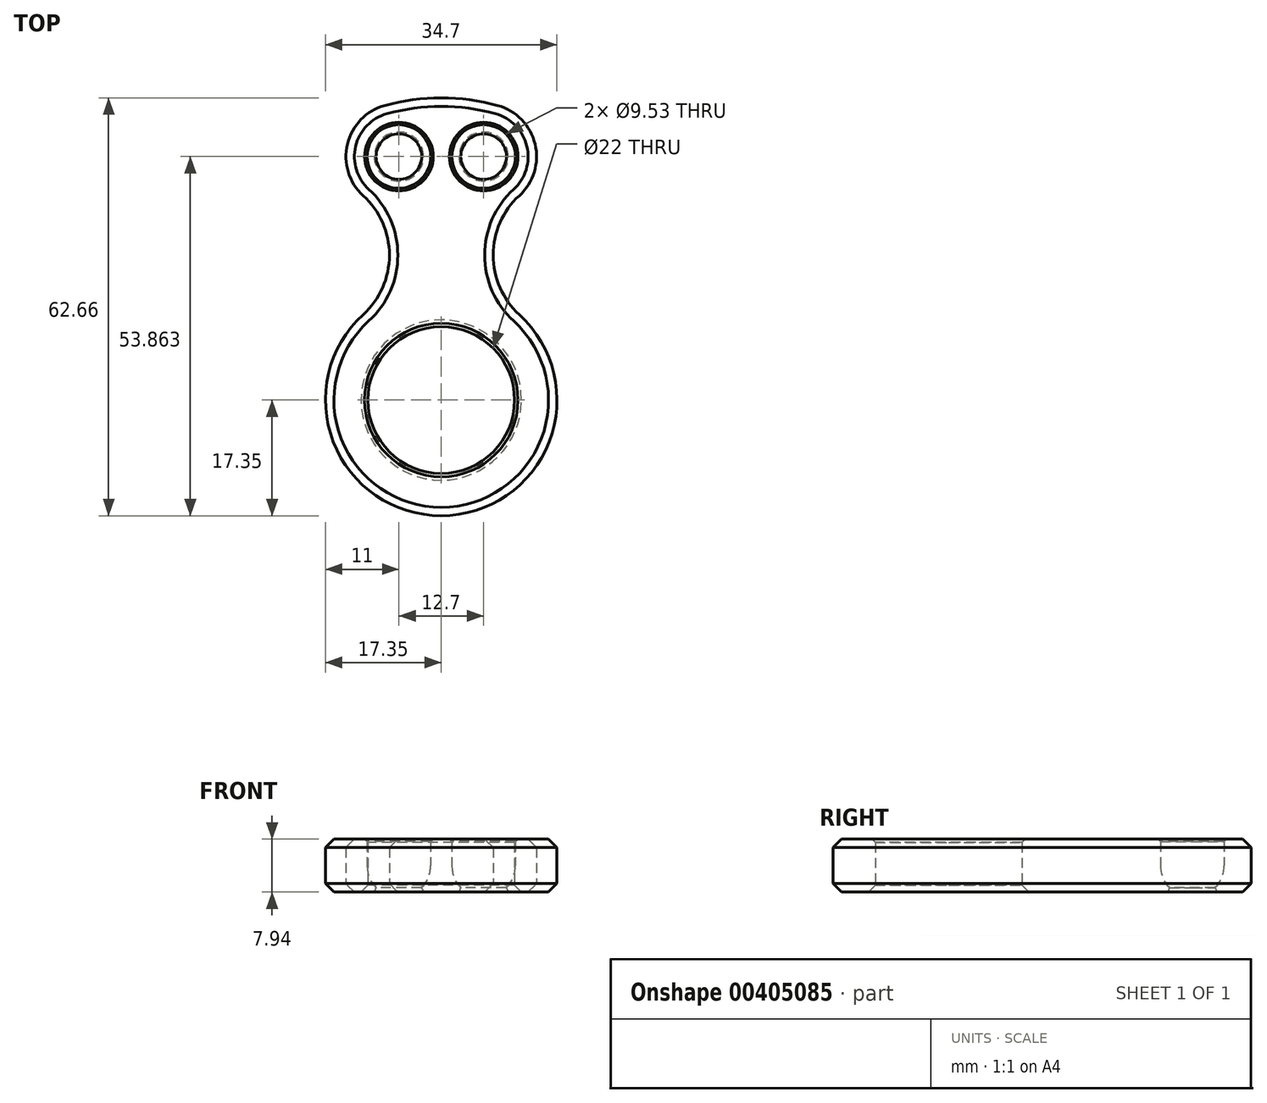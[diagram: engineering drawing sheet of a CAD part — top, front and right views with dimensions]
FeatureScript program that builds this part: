
annotation { "Feature Type Name" : "Feature", "Feature Type Description" : "" }
export const myFeature = defineFeature(function(context is Context, id is Id, definition is map)
    precondition{}
    {
        {
            var Q0;
            Q0=qCreatedBy(makeId("Top.planeOp"),FACE);
            var sketch = newSketch(context, id + "F0", { "sketchPlane" : qUnion([Q0])});
            skCircle(sketch, "E0", {"center": v(0, 0) * mm, "radius": 11 * mm});
            skCircle(sketch, "E1", {"center": v(0, 0) * mm, "radius": 17.35 * mm});
            skSolve(sketch);
        }
        {
            var Q0;
            Q0 = qSketchRegion(id + "F0", true);
            extrude(context, id + "F1", {"entities" : qUnion([Q0]), "depth" : 7.94 * mm});
        }
        {
            var Q0;
            Q0=qCreatedBy(makeId("Top.planeOp"),FACE);
            var sketch = newSketch(context, id + "F2", { "sketchPlane" : qUnion([Q0])});
            skCircle(sketch, "E2", {"center": v(-6.35, 36.51) * mm, "radius": 4.76 * mm});
            skArc(sketch, "E3.0", {"start": v(11.7, 12.8) * mm, "mid": v(0, 17.35) * mm, "end": v(-11.7, 12.8) * mm});
            skPoint(sketch, "E4", {"position": v(-6.35, 41.28) * mm});
            skCircle(sketch, "E5", {"center": v(6.35, 36.51) * mm, "radius": 4.76 * mm});
            skLineSegment(sketch, "E6", {"start": v(-6.35, 36.51) * mm, "end": v(6.35, 36.51) * mm, "construction": true});
            skLineSegment(sketch, "E7", {"start": v(0, 36.51) * mm, "end": v(0, 0) * mm, "construction": true});
            skLineSegment(sketch, "E8", {"start": v(-6.35, 41.28) * mm, "end": v(-6.35, 36.51) * mm, "construction": true});
            skArc(sketch, "E9", {"start": v(0, 31.75) * mm, "mid": v(1.59, 36.51) * mm, "end": v(0, 41.28) * mm, "construction": true});
            skArc(sketch, "E10", {"start": v(11.7, 30.65) * mm, "mid": v(14.07, 38.36) * mm, "end": v(8.47, 44.16) * mm});
            skArc(sketch, "E11", {"start": v(-11.7, 12.8) * mm, "mid": v(-7.77, 21.73) * mm, "end": v(-11.7, 30.65) * mm});
            skArc(sketch, "E12", {"start": v(11.7, 30.65) * mm, "mid": v(7.77, 21.73) * mm, "end": v(11.7, 12.8) * mm});
            skLineSegment(sketch, "E13", {"start": v(6.35, 36.51) * mm, "end": v(6.35, 41.28) * mm, "construction": true});
            skArc(sketch, "E14", {"start": v(8.47, 44.16) * mm, "mid": v(0, 45.31) * mm, "end": v(-8.47, 44.16) * mm});
            skArc(sketch, "E15.trimOffspring", {"start": v(-8.47, 44.16) * mm, "mid": v(-14.07, 38.36) * mm, "end": v(-11.7, 30.65) * mm});
            skArc(sketch, "E16.trimOffspring", {"start": v(0, 41.28) * mm, "mid": v(-1.59, 36.51) * mm, "end": v(0, 31.75) * mm, "construction": true});
            skSolve(sketch);
        }
        {
            var Q0;
            Q0 = qSketchRegion(id + "F2", true);
            var Q1;
            Q1=makeQuery(id+"F1.opExtrude","CAP_FACE",FACE,{"disambiguationData":[OSD([sQuery(id+"F0.wireOp",EDGE,"E0"),sQuery(id+"F0.wireOp",EDGE,"E1")])],"isStart":false});
            extrude(context, id + "F3", {"entities" : qUnion([Q0]), "operationType" : NewBodyOperationType.ADD, "endBound" : BoundingType.UP_TO_SURFACE, "endBoundEntityFace" : qUnion([Q1]), "depth" : 25.4 * mm});
        }
        {
            var Q0;
            Q0=qCreatedBy(makeId("Right.planeOp"),FACE);
            var Q1;
            Q1=sQuery(id+"F2.wireOp",VERTEX,"E6.start");
            cPlane(context, id + "F4", {"entities" : qUnion([Q0, Q1]), "cplaneType" : CPlaneType.PLANE_POINT, "offset" : 25.4 * mm, "width" : 152.4 * mm, "height" : 152.4 * mm});
        }
        {
            var Q0;
            Q0=qCreatedBy(makeId("Right.planeOp"),FACE);
            var Q1;
            Q1=sQuery(id+"F2.wireOp",VERTEX,"E6.end");
            cPlane(context, id + "F5", {"entities" : qUnion([Q0, Q1]), "cplaneType" : CPlaneType.PLANE_POINT, "offset" : 25.4 * mm, "width" : 152.4 * mm, "height" : 152.4 * mm});
        }
        {
            var Q0;
            Q0=qCreatedBy(id+"F4.planeOp",FACE);
            var sketch = newSketch(context, id + "F6", { "sketchPlane" : qUnion([Q0])});
            skArc(sketch, "E17", {"start": v(36.51, -0.8) * mm, "mid": v(37.89, -0.6) * mm, "end": v(39.15, 0) * mm, "construction": true});
            skLineSegment(sketch, "E18", {"start": v(41.28, 3.97) * mm, "end": v(41.28, 0) * mm});
            skLineSegment(sketch, "E19", {"start": v(36.51, 3.97) * mm, "end": v(36.51, 0) * mm, "construction": true});
            skLineSegment(sketch, "E20", {"start": v(0, 7.94) * mm, "end": v(0, 0) * mm, "construction": true});
            skLineSegment(sketch, "E21", {"start": v(0, 3.97) * mm, "end": v(36.51, 3.97) * mm, "construction": true});
            skLineSegment(sketch, "E22", {"start": v(39.15, 0) * mm, "end": v(41.28, 0) * mm});
            skArc(sketch, "E23", {"start": v(39.15, 0) * mm, "mid": v(40.7, 1.72) * mm, "end": v(41.28, 3.97) * mm});
            skSolve(sketch);
        }
        {
            var Q0;
            Q0 = qSketchRegion(id + "F6", true);
            var Q1;
            Q1=sQuery(id+"F6.wireOp",EDGE,"E19");
            revolve(context, id + "F7", {"operationType" : NewBodyOperationType.ADD, "entities" : qUnion([Q0]), "axis" : qUnion([Q1]), "revolveType" : RevolveType.FULL});
        }
        {
            var Q0;
            Q0=qCreatedBy(id+"F5.planeOp",FACE);
            var sketch = newSketch(context, id + "F8", { "sketchPlane" : qUnion([Q0])});
            skArc(sketch, "E24.0", {"start": v(39.15, 0) * mm, "mid": v(40.7, 1.72) * mm, "end": v(41.28, 3.97) * mm});
            skLineSegment(sketch, "E24.1", {"start": v(41.28, 3.97) * mm, "end": v(41.28, 0) * mm});
            skLineSegment(sketch, "E24.2", {"start": v(36.51, 3.97) * mm, "end": v(36.51, 0) * mm, "construction": true});
            skLineSegment(sketch, "E24.3", {"start": v(39.15, 0) * mm, "end": v(41.28, 0) * mm});
            skSolve(sketch);
        }
        {
            var Q0;
            Q0 = qSketchRegion(id + "F8", true);
            var Q1;
            Q1=sQuery(id+"F8.wireOp",EDGE,"E24.2");
            var Q2;
            Q2=sQuery(id+"F8.wireOp",EDGE,"E24.3");
            var Q3;
            Q3=sQuery(id+"F8.wireOp",EDGE,"E24.0");
            var Q4;
            Q4=sQuery(id+"F8.wireOp",EDGE,"E24.1");
            var Q5;
            Q5=sQuery(id+"F8.wireOp",EDGE,"E24.2");
            revolve(context, id + "F9", {"operationType" : NewBodyOperationType.ADD, "entities" : qUnion([Q0]), "surfaceEntities" : qUnion([Q1, Q2, Q3, Q4]), "axis" : qUnion([Q5]), "revolveType" : RevolveType.FULL});
        }
        {
            var Q0;
            Q0=qCreatedBy(makeId("Right.planeOp"),FACE);
            var sketch = newSketch(context, id + "F10", { "sketchPlane" : qUnion([Q0])});
            skLineSegment(sketch, "E25", {"start": v(0, 0) * mm, "end": v(0, 7.94) * mm});
            skSolve(sketch);
        }
        {
            var Q0;
            Q0=makeQuery(id+"FtfaqkLsv2ppWGT_1.2.F3.opExtrude","SWEPT_FACE",FACE,{"disambiguationData":[OSD([sQuery(id+"F2.wireOp",EDGE,"GdqiwVMI-0yTA-f3Nu-G5DB-PIxRIdhKu170")])]});
            var Q1;
            {var subQ0=sQuery(id+"F0.wireOp",EDGE,"E1");var subQ6=sQuery(id+"F2.wireOp",EDGE,"91fbf01b-bf65-43be-b05c-4fdd76e7d2ed0.MirrorCS");var subQ7=sQuery(id+"F2.wireOp",EDGE,"GdqiwVMI-0yTA-f3Nu-G5DB-PIxRIdhKu170");var subQ11=makeQuery(id+"FtfaqkLsv2ppWGT_1.1.F3.opExtrude","SWEPT_FACE",FACE,{"disambiguationData":[OSD([subQ6])]});Q1=makeQuery(id+"FtfaqkLsv2ppWGT_1.2.F3.boolean.opBoolean","SPLIT",FACE,{"disambiguationData":[TD([subQ11])],"derivedFrom":makeQuery(id+"FtfaqkLsv2ppWGT_1.1.F3.boolean.opBoolean","SPLIT",FACE,{"disambiguationData":[TD([makeQuery(id+"F3.opExtrude","SWEPT_FACE",FACE,{"disambiguationData":[OSD([subQ7])]})])],"derivedFrom":makeQuery(id+"F1.opExtrude","SWEPT_FACE",FACE,{"disambiguationData":[OSD([subQ0])]})})});}
            var Q2;
            Q2=makeQuery(id+"FtfaqkLsv2ppWGT_1.1.F3.opExtrude","SWEPT_FACE",FACE,{"disambiguationData":[OSD([sQuery(id+"F2.wireOp",EDGE,"91fbf01b-bf65-43be-b05c-4fdd76e7d2ed0.MirrorCS")])]});
            var Q3;
            Q3=makeQuery(id+"FtfaqkLsv2ppWGT_1.1.F3.opExtrude","SWEPT_FACE",FACE,{"disambiguationData":[OSD([sQuery(id+"F2.wireOp",EDGE,"UisbAJZM-tnmu-mLXv-kcAc-P8EMrq4znzEN")])]});
            var Q4;
            Q4=makeQuery(id+"FtfaqkLsv2ppWGT_1.2.F3.opExtrude","SWEPT_FACE",FACE,{"disambiguationData":[OSD([sQuery(id+"F2.wireOp",EDGE,"UisbAJZM-tnmu-mLXv-kcAc-P8EMrq4znzEN")])]});
            var Q5;
            Q5=makeQuery(id+"FtfaqkLsv2ppWGT_1.2.F3.opExtrude","SWEPT_FACE",FACE,{"disambiguationData":[OSD([sQuery(id+"F2.wireOp",EDGE,"91fbf01b-bf65-43be-b05c-4fdd76e7d2ed0.MirrorCS")])]});
            var Q6;
            {var subQ0=sQuery(id+"F0.wireOp",EDGE,"E1");var subQ7=sQuery(id+"F2.wireOp",EDGE,"GdqiwVMI-0yTA-f3Nu-G5DB-PIxRIdhKu170");var subQ11=makeQuery(id+"F3.opExtrude","SWEPT_FACE",FACE,{"disambiguationData":[OSD([subQ7])]});Q6=makeQuery(id+"FtfaqkLsv2ppWGT_1.2.F3.boolean.opBoolean","SPLIT",FACE,{"disambiguationData":[TD([subQ11])],"derivedFrom":makeQuery(id+"FtfaqkLsv2ppWGT_1.1.F3.boolean.opBoolean","SPLIT",FACE,{"disambiguationData":[TD([subQ11])],"derivedFrom":makeQuery(id+"F1.opExtrude","SWEPT_FACE",FACE,{"disambiguationData":[OSD([subQ0])]})})});}
            var Q7;
            Q7=makeQuery(id+"F3.opExtrude","SWEPT_FACE",FACE,{"disambiguationData":[OSD([sQuery(id+"F2.wireOp",EDGE,"GdqiwVMI-0yTA-f3Nu-G5DB-PIxRIdhKu170")])]});
            var Q8;
            Q8=makeQuery(id+"F3.opExtrude","SWEPT_FACE",FACE,{"disambiguationData":[OSD([sQuery(id+"F2.wireOp",EDGE,"UisbAJZM-tnmu-mLXv-kcAc-P8EMrq4znzEN")])]});
            var Q9;
            Q9=makeQuery(id+"F3.opExtrude","SWEPT_FACE",FACE,{"disambiguationData":[OSD([sQuery(id+"F2.wireOp",EDGE,"91fbf01b-bf65-43be-b05c-4fdd76e7d2ed0.MirrorCS")])]});
            var Q10;
            Q10=makeQuery(id+"FtfaqkLsv2ppWGT_1.1.F3.opExtrude","SWEPT_FACE",FACE,{"disambiguationData":[OSD([sQuery(id+"F2.wireOp",EDGE,"GdqiwVMI-0yTA-f3Nu-G5DB-PIxRIdhKu170")])]});
            var Q11;
            {var subQ1=sQuery(id+"F2.wireOp",EDGE,"91fbf01b-bf65-43be-b05c-4fdd76e7d2ed0.MirrorCS");var subQ5=sQuery(id+"F0.wireOp",EDGE,"E1");Q11=makeQuery(id+"FtfaqkLsv2ppWGT_1.1.F3.boolean.opBoolean","SPLIT",FACE,{"disambiguationData":[TD([makeQuery(id+"F3.opExtrude","SWEPT_FACE",FACE,{"disambiguationData":[OSD([subQ1])]})])],"derivedFrom":makeQuery(id+"F1.opExtrude","SWEPT_FACE",FACE,{"disambiguationData":[OSD([subQ5])]})});}
            var Q12;
            Q12=makeQuery(id+"F3.opExtrude","SWEPT_FACE",FACE,{"disambiguationData":[OSD([sQuery(id+"F2.wireOp",EDGE,"E11")])]});
            var Q13;
            Q13=makeQuery(id+"F3.opExtrude","SWEPT_FACE",FACE,{"disambiguationData":[OSD([sQuery(id+"F2.wireOp",EDGE,"E15.trimOffspring")])]});
            var Q14;
            Q14=makeQuery(id+"F3.opExtrude","SWEPT_FACE",FACE,{"disambiguationData":[OSD([sQuery(id+"F2.wireOp",EDGE,"E14")])]});
            chamfer(context, id + "F11", {"entities" : qUnion([Q0, Q1, Q2, Q3, Q4, Q5, Q6, Q7, Q8, Q9, Q10, Q11, Q12, Q13, Q14]), "width" : 1.27 * mm, "tangentPropagation" : true});
        }
        {
            var Q0;
            Q0=makeQuery(id+"F1.opExtrude","CAP_EDGE",EDGE,{"disambiguationData":[OSD([sQuery(id+"F0.wireOp",EDGE,"E0")])],"isStart":false});
            chamfer(context, id + "F12", {"entities" : qUnion([Q0]), "width" : 0.5 * mm, "tangentPropagation" : true});
        }
        {
            var Q0;
            Q0=makeQuery(id+"F1.opExtrude","CAP_EDGE",EDGE,{"disambiguationData":[OSD([sQuery(id+"F0.wireOp",EDGE,"E0")])],"isStart":true});
            chamfer(context, id + "F13", {"entities" : qUnion([Q0]), "width" : 1.02 * mm, "tangentPropagation" : true});
        }
        {
            var Q0;
            Q0=makeQuery(id+"FtfaqkLsv2ppWGT_1.2.F7.opRevolve","SWEPT_EDGE",EDGE,{"disambiguationData":[OSD([sQuery(id+"F6.wireOp",EDGE,"E22"),sQuery(id+"F6.wireOp",EDGE,"E23")])]});
            var Q1;
            Q1=makeQuery(id+"FtfaqkLsv2ppWGT_1.2.F9.opRevolve","SWEPT_EDGE",EDGE,{"disambiguationData":[OSD([sQuery(id+"F8.wireOp",EDGE,"E24.0"),sQuery(id+"F8.wireOp",EDGE,"E24.3")])]});
            var Q2;
            Q2=makeQuery(id+"F9.opRevolve","SWEPT_EDGE",EDGE,{"disambiguationData":[OSD([sQuery(id+"F8.wireOp",EDGE,"E24.0"),sQuery(id+"F8.wireOp",EDGE,"E24.3")])]});
            var Q3;
            Q3=makeQuery(id+"F7.opRevolve","SWEPT_EDGE",EDGE,{"disambiguationData":[OSD([sQuery(id+"F6.wireOp",EDGE,"E22"),sQuery(id+"F6.wireOp",EDGE,"E23")])]});
            var Q4;
            Q4=makeQuery(id+"FtfaqkLsv2ppWGT_1.1.F9.opRevolve","SWEPT_EDGE",EDGE,{"disambiguationData":[OSD([sQuery(id+"F8.wireOp",EDGE,"E24.0"),sQuery(id+"F8.wireOp",EDGE,"E24.3")])]});
            var Q5;
            Q5=makeQuery(id+"FtfaqkLsv2ppWGT_1.1.F7.opRevolve","SWEPT_EDGE",EDGE,{"disambiguationData":[OSD([sQuery(id+"F6.wireOp",EDGE,"E22"),sQuery(id+"F6.wireOp",EDGE,"E23")])]});
            var Q6;
            Q6=makeQuery(id+"FtfaqkLsv2ppWGT_1.2.F3.opExtrude","CAP_EDGE",EDGE,{"disambiguationData":[OSD([sQuery(id+"F2.wireOp",EDGE,"E5")])],"isStart":false});
            var Q7;
            Q7=makeQuery(id+"FtfaqkLsv2ppWGT_1.2.F3.opExtrude","CAP_EDGE",EDGE,{"disambiguationData":[OSD([sQuery(id+"F2.wireOp",EDGE,"E2")])],"isStart":false});
            var Q8;
            Q8=makeQuery(id+"F3.opExtrude","CAP_EDGE",EDGE,{"disambiguationData":[OSD([sQuery(id+"F2.wireOp",EDGE,"E5")])],"isStart":false});
            var Q9;
            Q9=makeQuery(id+"F3.opExtrude","CAP_EDGE",EDGE,{"disambiguationData":[OSD([sQuery(id+"F2.wireOp",EDGE,"E2")])],"isStart":false});
            var Q10;
            Q10=makeQuery(id+"FtfaqkLsv2ppWGT_1.1.F3.opExtrude","CAP_EDGE",EDGE,{"disambiguationData":[OSD([sQuery(id+"F2.wireOp",EDGE,"E2")])],"isStart":false});
            var Q11;
            Q11=makeQuery(id+"FtfaqkLsv2ppWGT_1.1.F3.opExtrude","CAP_EDGE",EDGE,{"disambiguationData":[OSD([sQuery(id+"F2.wireOp",EDGE,"E5")])],"isStart":false});
            chamfer(context, id + "F14", {"entities" : qUnion([Q0, Q1, Q2, Q3, Q4, Q5, Q6, Q7, Q8, Q9, Q10, Q11]), "width" : 0.38 * mm, "tangentPropagation" : true});
        }
    });
